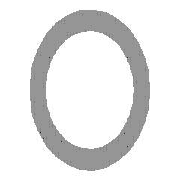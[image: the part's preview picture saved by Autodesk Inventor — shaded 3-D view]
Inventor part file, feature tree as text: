
AUTODESK INVENTOR PART (.ipt)
format: ipt  version: 2021 (Build 250183000, 183)  size: 270,848 bytes
history: native  units: mm (DEFAULTED — no unit token found)
features: other x9, plane x8, sketch x4, extrude x2, sweep x1
ambient origin geometry x8: Origin, YZ Plane, XZ Plane, XY Plane, X Axis, Y Axis, Z Axis, Center Point
bodies: Solid1 (feature_tree)
feature tree (24):
  parser-record x1  (decoder bookkeeping rows leaked as tree rows — omitted from the tree; the rows remain in map.json)
  other  "Driven Length"
  other  "Plano inicial"
  other  "Plano final"
  other  "Trayectoria de barrido"
  plane  "Plano de trabajo de orientación"
  sweep  "Cuerpo"
  plane  "Plano de trabajo5"
  plane  "Plano de trabajo6"
  plane  "Plano de trabajo7"
  extrude  "Extrusión2"  Depth=752.259455mm
  other  "Combinar1"
  plane  "Plano de trabajo8"
  plane  "Plano de trabajo9"
  plane  "Plano de trabajo10"
  extrude  "Extrusión3"  Depth=752.259455mm
  other  "Combinar2"
  sketch  "Sketch3"  dims[d0=33.528mm d1=4.5466mm]
  plane  "Work Plane3"
  sketch  "Sketch4"  dims[d4=-0.0mm d5=752.259455mm]
  sketch  "Boceto5"  dims[d6=90.0deg d7=752.259455mm]
  other  "Sólido2"
  sketch  "Boceto6"  dims[d8=0.0mm d9=0.0mm d10=0.12mm d11=0.0mm d12=0.12mm d13=0.0mm]
  other  "Sólido3"
